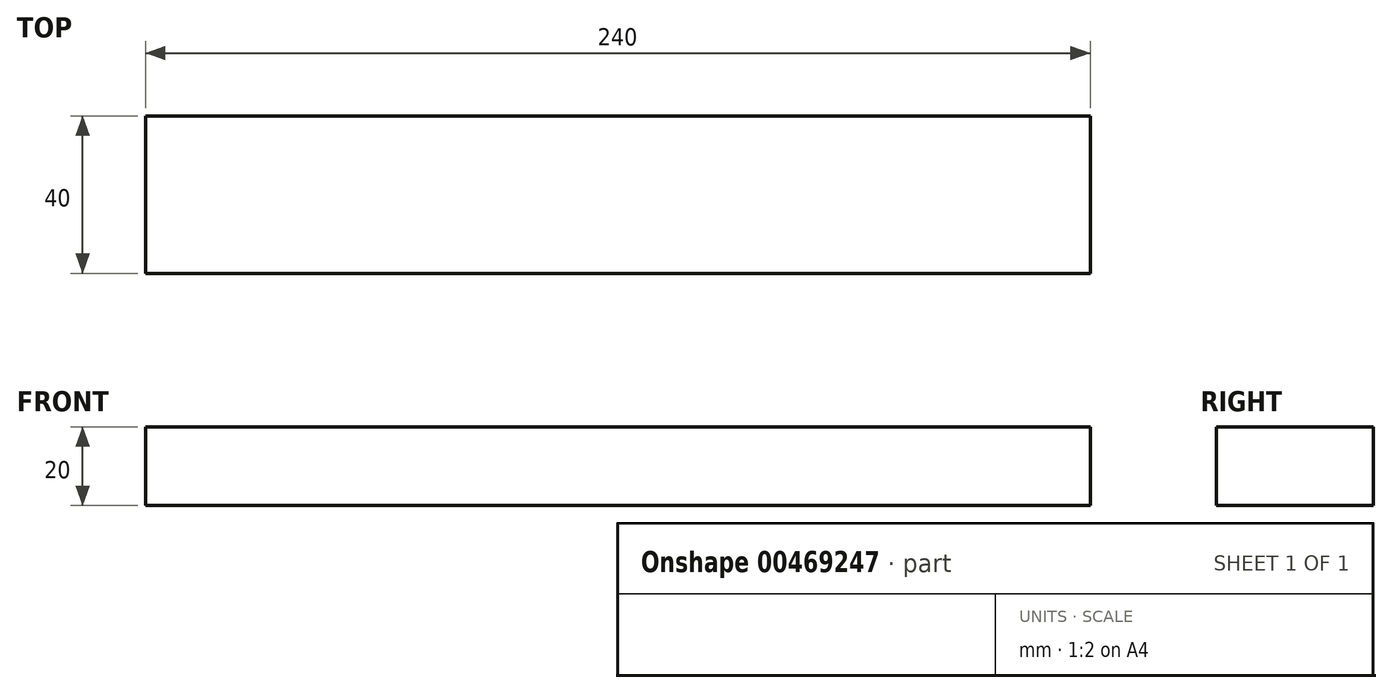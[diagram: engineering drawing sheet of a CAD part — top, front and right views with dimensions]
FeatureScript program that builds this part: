
annotation { "Feature Type Name" : "Feature", "Feature Type Description" : "" }
export const myFeature = defineFeature(function(context is Context, id is Id, definition is map)
    precondition{}
    {
        {
            var Q0;
            Q0=qCreatedBy(makeId("Top.planeOp"),FACE);
            var sketch = newSketch(context, id + "F0", { "sketchPlane" : qUnion([Q0])});
            skLineSegment(sketch, "E0.bottom", {"start": v(-120, -20) * mm, "end": v(120, -20) * mm});
            skLineSegment(sketch, "E0.top", {"start": v(-120, 20) * mm, "end": v(120, 20) * mm});
            skLineSegment(sketch, "E0.left", {"start": v(-120, -20) * mm, "end": v(-120, 20) * mm});
            skLineSegment(sketch, "E0.right", {"start": v(120, -20) * mm, "end": v(120, 20) * mm});
            skPoint(sketch, "E0.middle", {"position": v(0, 0) * mm});
            skSolve(sketch);
        }
        {
            var Q0;
            Q0=makeQuery(id+"F0.imprint","IMPRINT",FACE,{"disambiguationData":[TD([[makeQuery(id+"F0.imprint","IMPRINT",EDGE,{"derivedFrom":sQuery(id+"F0.wireOp",EDGE,"E0.bottom")}),1.0]])]});
            extrude(context, id + "F1", {"entities" : qUnion([Q0]), "endBound" : BoundingType.SYMMETRIC, "depth" : 20 * mm});
        }
    });
